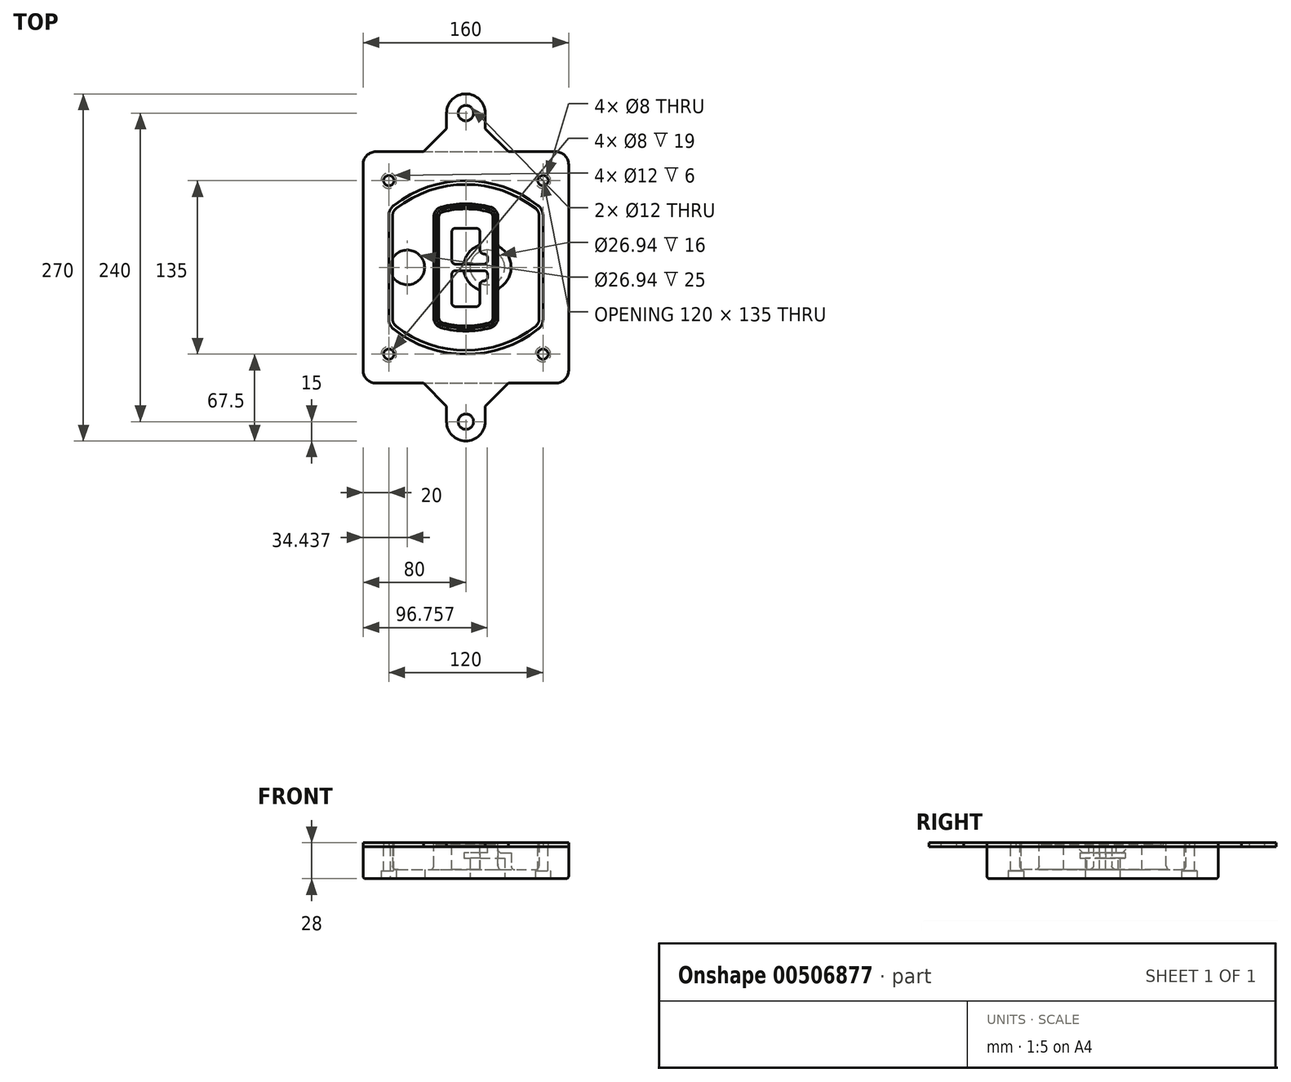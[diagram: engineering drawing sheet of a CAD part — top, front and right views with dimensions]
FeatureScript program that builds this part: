
annotation { "Feature Type Name" : "Feature", "Feature Type Description" : "" }
export const myFeature = defineFeature(function(context is Context, id is Id, definition is map)
    precondition{}
    {
        {
            var Q0;
            Q0=qCreatedBy(makeId("Top.planeOp"),FACE);
            var sketch = newSketch(context, id + "F0", { "sketchPlane" : qUnion([Q0])});
            skPoint(sketch, "E0.rect.middle", {"position": v(0, 0) * mm});
            skLineSegment(sketch, "E1.bottom", {"start": v(-70, -90) * mm, "end": v(70, -90) * mm});
            skLineSegment(sketch, "E1.top", {"start": v(-70, 90) * mm, "end": v(70, 90) * mm});
            skLineSegment(sketch, "E1.left", {"start": v(-80, -80) * mm, "end": v(-80, 80) * mm});
            skLineSegment(sketch, "E1.right", {"start": v(80, -80) * mm, "end": v(80, 80) * mm});
            skLineSegment(sketch, "E2", {"start": v(-80, 90) * mm, "end": v(80, -90) * mm, "construction": true});
            skLineSegment(sketch, "E3", {"start": v(80, 90) * mm, "end": v(-80, -90) * mm, "construction": true});
            skCircle(sketch, "E4", {"center": v(-60, 67.5) * mm, "radius": 4 * mm});
            skCircle(sketch, "E5", {"center": v(60, 67.5) * mm, "radius": 4 * mm});
            skCircle(sketch, "E6", {"center": v(60, -67.5) * mm, "radius": 4 * mm});
            skCircle(sketch, "E7", {"center": v(-60, -67.5) * mm, "radius": 4 * mm});
            skLineSegment(sketch, "E8", {"start": v(-60, 67.5) * mm, "end": v(60, 67.5) * mm, "construction": true});
            skLineSegment(sketch, "E9", {"start": v(60, 67.5) * mm, "end": v(60, -67.5) * mm, "construction": true});
            skLineSegment(sketch, "E10", {"start": v(60, -67.5) * mm, "end": v(-60, -67.5) * mm, "construction": true});
            skLineSegment(sketch, "E11", {"start": v(-60, -67.5) * mm, "end": v(-60, 67.5) * mm, "construction": true});
            skLineSegment(sketch, "E12", {"start": v(-60, 40.3) * mm, "end": v(-60, -40.3) * mm});
            skLineSegment(sketch, "E13", {"start": v(60, 40.3) * mm, "end": v(60, -40.3) * mm});
            skArc(sketch, "E14", {"start": v(56.15, 48.18) * mm, "mid": v(0, 67.5) * mm, "end": v(-56.15, 48.18) * mm});
            skArc(sketch, "E15", {"start": v(-56.15, -48.18) * mm, "mid": v(0, -67.5) * mm, "end": v(56.15, -48.18) * mm});
            skLineSegment(sketch, "E16", {"start": v(-60, 0) * mm, "end": v(60, 0) * mm, "construction": true});
            skPoint(sketch, "E17.visualSharp", {"position": v(-60, -45) * mm});
            skArc(sketch, "E17.filletArc", {"start": v(-60, -40.3) * mm, "mid": v(-58.99, -44.68) * mm, "end": v(-56.15, -48.18) * mm});
            skPoint(sketch, "E18.visualSharp", {"position": v(-60, 45) * mm});
            skArc(sketch, "E18.filletArc", {"start": v(-56.15, 48.18) * mm, "mid": v(-58.99, 44.68) * mm, "end": v(-60, 40.3) * mm});
            skPoint(sketch, "E19.visualSharp", {"position": v(60, 45) * mm});
            skArc(sketch, "E19.filletArc", {"start": v(60, 40.3) * mm, "mid": v(58.99, 44.68) * mm, "end": v(56.15, 48.18) * mm});
            skPoint(sketch, "E20.visualSharp", {"position": v(60, -45) * mm});
            skArc(sketch, "E20.filletArc", {"start": v(56.15, -48.18) * mm, "mid": v(58.99, -44.68) * mm, "end": v(60, -40.3) * mm});
            skPoint(sketch, "E21.visualSharp", {"position": v(-80, 90) * mm});
            skArc(sketch, "E21.filletArc", {"start": v(-70, 90) * mm, "mid": v(-77.07, 87.07) * mm, "end": v(-80, 80) * mm});
            skPoint(sketch, "E22.visualSharp", {"position": v(80, 90) * mm});
            skArc(sketch, "E22.filletArc", {"start": v(80, 80) * mm, "mid": v(77.07, 87.07) * mm, "end": v(70, 90) * mm});
            skPoint(sketch, "E23.visualSharp", {"position": v(80, -90) * mm});
            skArc(sketch, "E23.filletArc", {"start": v(70, -90) * mm, "mid": v(77.07, -87.07) * mm, "end": v(80, -80) * mm});
            skPoint(sketch, "E24.visualSharp", {"position": v(-80, -90) * mm});
            skArc(sketch, "E24.filletArc", {"start": v(-80, -80) * mm, "mid": v(-77.07, -87.07) * mm, "end": v(-70, -90) * mm});
            skArc(sketch, "E25.0", {"start": v(57, 40.3) * mm, "mid": v(56.3, 43.36) * mm, "end": v(54.3, 45.81) * mm});
            skLineSegment(sketch, "E25.1", {"start": v(57, 40.3) * mm, "end": v(57, -40.3) * mm});
            skArc(sketch, "E25.2", {"start": v(54.3, -45.81) * mm, "mid": v(56.3, -43.36) * mm, "end": v(57, -40.3) * mm});
            skArc(sketch, "E25.3", {"start": v(-54.3, -45.81) * mm, "mid": v(0, -64.5) * mm, "end": v(54.3, -45.81) * mm});
            skArc(sketch, "E25.4", {"start": v(-57, -40.3) * mm, "mid": v(-56.3, -43.36) * mm, "end": v(-54.3, -45.81) * mm});
            skArc(sketch, "E25.5", {"start": v(54.3, 45.81) * mm, "mid": v(0, 64.5) * mm, "end": v(-54.3, 45.81) * mm});
            skLineSegment(sketch, "E25.6", {"start": v(-57, 40.3) * mm, "end": v(-57, -40.3) * mm});
            skArc(sketch, "E25.7", {"start": v(-54.3, 45.81) * mm, "mid": v(-56.3, 43.36) * mm, "end": v(-57, 40.3) * mm});
            skArc(sketch, "E26.0", {"start": v(-58.62, 51.33) * mm, "mid": v(-62.58, 46.43) * mm, "end": v(-64, 40.3) * mm});
            skArc(sketch, "E26.1", {"start": v(58.62, 51.33) * mm, "mid": v(0, 71.5) * mm, "end": v(-58.62, 51.33) * mm});
            skArc(sketch, "E26.2", {"start": v(64, 40.3) * mm, "mid": v(62.58, 46.43) * mm, "end": v(58.62, 51.33) * mm});
            skLineSegment(sketch, "E26.3", {"start": v(64, 40.3) * mm, "end": v(64, -40.3) * mm});
            skArc(sketch, "E26.4", {"start": v(58.62, -51.33) * mm, "mid": v(62.58, -46.43) * mm, "end": v(64, -40.3) * mm});
            skLineSegment(sketch, "E26.5", {"start": v(-64, 40.3) * mm, "end": v(-64, -40.3) * mm});
            skArc(sketch, "E26.6", {"start": v(-58.62, -51.33) * mm, "mid": v(0, -71.5) * mm, "end": v(58.62, -51.33) * mm});
            skArc(sketch, "E26.7", {"start": v(-64, -40.3) * mm, "mid": v(-62.58, -46.43) * mm, "end": v(-58.62, -51.33) * mm});
            skSolve(sketch);
        }
        {
            var Q0;
            Q0=makeQuery(id+"F0.imprint","IMPRINT",FACE,{"disambiguationData":[TD([[makeQuery(id+"F0.imprint","IMPRINT",EDGE,{"derivedFrom":sQuery(id+"F0.wireOp",EDGE,"E1.bottom")}),1.0]])]});
            var Q1;
            Q1=makeQuery(id+"F0.imprint","IMPRINT",FACE,{"disambiguationData":[TD([[makeQuery(id+"F0.imprint","IMPRINT",EDGE,{"derivedFrom":sQuery(id+"F0.wireOp",EDGE,"E12")}),1.0]])]});
            var Q2;
            Q2=makeQuery(id+"F0.imprint","IMPRINT",FACE,{"disambiguationData":[TD([[makeQuery(id+"F0.imprint","IMPRINT",EDGE,{"derivedFrom":sQuery(id+"F0.wireOp",EDGE,"E25.0")}),1.0]])]});
            var Q3;
            Q3=makeQuery(id+"F0.imprint","IMPRINT",FACE,{"disambiguationData":[TD([[makeQuery(id+"F0.imprint","IMPRINT",EDGE,{"derivedFrom":sQuery(id+"F0.wireOp",EDGE,"E12")}),-1.0]])]});
            extrude(context, id + "F1", {"entities" : qUnion([Q0, Q1, Q2, Q3]), "oppositeDirection" : true, "depth" : 25 * mm});
        }
        {
            var Q0;
            Q0=makeQuery(id+"F0.imprint","IMPRINT",FACE,{"disambiguationData":[TD([[makeQuery(id+"F0.imprint","IMPRINT",EDGE,{"derivedFrom":sQuery(id+"F0.wireOp",EDGE,"E12")}),1.0]])]});
            extrude(context, id + "F2", {"entities" : qUnion([Q0]), "operationType" : NewBodyOperationType.ADD, "depth" : 3 * mm});
        }
        {
            var Q0;
            Q0=makeQuery(id+"F0.imprint","IMPRINT",FACE,{"disambiguationData":[TD([[makeQuery(id+"F0.imprint","IMPRINT",EDGE,{"derivedFrom":sQuery(id+"F0.wireOp",EDGE,"E25.0")}),1.0]])]});
            extrude(context, id + "F3", {"entities" : qUnion([Q0]), "operationType" : NewBodyOperationType.REMOVE, "oppositeDirection" : true, "depth" : 18 * mm});
        }
        {
            var Q0;
            Q0=makeQuery(id+"F2.opExtrude","CAP_FACE",FACE,{"disambiguationData":[OSD([sQuery(id+"F0.wireOp",EDGE,"E12"),sQuery(id+"F0.wireOp",EDGE,"E13"),sQuery(id+"F0.wireOp",EDGE,"E14"),sQuery(id+"F0.wireOp",EDGE,"E15"),sQuery(id+"F0.wireOp",EDGE,"E17.filletArc"),sQuery(id+"F0.wireOp",EDGE,"E18.filletArc"),sQuery(id+"F0.wireOp",EDGE,"E19.filletArc"),sQuery(id+"F0.wireOp",EDGE,"E20.filletArc"),sQuery(id+"F0.wireOp",EDGE,"E25.0"),sQuery(id+"F0.wireOp",EDGE,"E25.1"),sQuery(id+"F0.wireOp",EDGE,"E25.2"),sQuery(id+"F0.wireOp",EDGE,"E25.3"),sQuery(id+"F0.wireOp",EDGE,"E25.4"),sQuery(id+"F0.wireOp",EDGE,"E25.5"),sQuery(id+"F0.wireOp",EDGE,"E25.6"),sQuery(id+"F0.wireOp",EDGE,"E25.7")])],"isStart":false});
            var sketch = newSketch(context, id + "F4", { "sketchPlane" : qUnion([Q0])});
            skArc(sketch, "E27.0", {"start": v(-19.08, -46.97) * mm, "mid": v(0, -49.5) * mm, "end": v(19.08, -46.97) * mm});
            skArc(sketch, "E28.0", {"start": v(19.08, 46.97) * mm, "mid": v(0, 49.5) * mm, "end": v(-19.08, 46.97) * mm});
            skLineSegment(sketch, "E29", {"start": v(-25, 39.25) * mm, "end": v(-25, -39.25) * mm});
            skLineSegment(sketch, "E30", {"start": v(25, 39.25) * mm, "end": v(25, -39.25) * mm});
            skLineSegment(sketch, "E31", {"start": v(-25, 45.1) * mm, "end": v(25, 45.1) * mm, "construction": true});
            skLineSegment(sketch, "E32", {"start": v(-25, -45.1) * mm, "end": v(25, -45.1) * mm, "construction": true});
            skPoint(sketch, "E33.visualSharp", {"position": v(-25, 45.1) * mm});
            skArc(sketch, "E33.filletArc", {"start": v(-19.08, 46.97) * mm, "mid": v(-23.35, 44.11) * mm, "end": v(-25, 39.25) * mm});
            skPoint(sketch, "E34.visualSharp", {"position": v(25, 45.1) * mm});
            skArc(sketch, "E34.filletArc", {"start": v(25, 39.25) * mm, "mid": v(23.35, 44.11) * mm, "end": v(19.08, 46.97) * mm});
            skPoint(sketch, "E35.visualSharp", {"position": v(25, -45.1) * mm});
            skArc(sketch, "E35.filletArc", {"start": v(19.08, -46.97) * mm, "mid": v(23.35, -44.11) * mm, "end": v(25, -39.25) * mm});
            skPoint(sketch, "E36.visualSharp", {"position": v(-25, -45.1) * mm});
            skArc(sketch, "E36.filletArc", {"start": v(-25, -39.25) * mm, "mid": v(-23.35, -44.11) * mm, "end": v(-19.08, -46.97) * mm});
            skArc(sketch, "E37.0", {"start": v(54.3, 45.81) * mm, "mid": v(0, 64.5) * mm, "end": v(-54.3, 45.81) * mm});
            skArc(sketch, "E37.1", {"start": v(-54.3, 45.81) * mm, "mid": v(-56.3, 43.36) * mm, "end": v(-57, 40.3) * mm});
            skLineSegment(sketch, "E37.2", {"start": v(-57, 40.3) * mm, "end": v(-57, -40.3) * mm});
            skArc(sketch, "E37.3", {"start": v(-57, -40.3) * mm, "mid": v(-56.3, -43.36) * mm, "end": v(-54.3, -45.81) * mm});
            skArc(sketch, "E37.4", {"start": v(-54.3, -45.81) * mm, "mid": v(0, -64.5) * mm, "end": v(54.3, -45.81) * mm});
            skArc(sketch, "E37.5", {"start": v(54.3, -45.81) * mm, "mid": v(56.3, -43.36) * mm, "end": v(57, -40.3) * mm});
            skLineSegment(sketch, "E37.6", {"start": v(57, 40.3) * mm, "end": v(57, -40.3) * mm});
            skArc(sketch, "E37.7", {"start": v(57, 40.3) * mm, "mid": v(56.3, 43.36) * mm, "end": v(54.3, 45.81) * mm});
            skLineSegment(sketch, "E38.0", {"start": v(23, 39.25) * mm, "end": v(23, -39.25) * mm});
            skArc(sketch, "E38.1", {"start": v(18.56, -45.04) * mm, "mid": v(21.76, -42.9) * mm, "end": v(23, -39.25) * mm});
            skArc(sketch, "E38.2", {"start": v(-18.56, -45.04) * mm, "mid": v(0, -47.5) * mm, "end": v(18.56, -45.04) * mm});
            skArc(sketch, "E38.3", {"start": v(-23, -39.25) * mm, "mid": v(-21.76, -42.9) * mm, "end": v(-18.56, -45.04) * mm});
            skLineSegment(sketch, "E38.4", {"start": v(-23, 39.25) * mm, "end": v(-23, -39.25) * mm});
            skArc(sketch, "E38.5", {"start": v(23, 39.25) * mm, "mid": v(21.76, 42.9) * mm, "end": v(18.56, 45.04) * mm});
            skArc(sketch, "E38.6", {"start": v(-18.56, 45.04) * mm, "mid": v(-21.76, 42.9) * mm, "end": v(-23, 39.25) * mm});
            skArc(sketch, "E38.7", {"start": v(18.56, 45.04) * mm, "mid": v(0, 47.5) * mm, "end": v(-18.56, 45.04) * mm});
            skArc(sketch, "E39.0", {"start": v(21, 39.25) * mm, "mid": v(20.18, 41.68) * mm, "end": v(18.04, 43.1) * mm});
            skLineSegment(sketch, "E39.1", {"start": v(21, 39.25) * mm, "end": v(21, -39.25) * mm});
            skArc(sketch, "E39.2", {"start": v(18.04, -43.1) * mm, "mid": v(20.18, -41.68) * mm, "end": v(21, -39.25) * mm});
            skArc(sketch, "E39.3", {"start": v(-18.04, -43.1) * mm, "mid": v(0, -45.5) * mm, "end": v(18.04, -43.1) * mm});
            skArc(sketch, "E39.4", {"start": v(-21, -39.25) * mm, "mid": v(-20.18, -41.68) * mm, "end": v(-18.04, -43.1) * mm});
            skArc(sketch, "E39.5", {"start": v(18.04, 43.1) * mm, "mid": v(0, 45.5) * mm, "end": v(-18.04, 43.1) * mm});
            skLineSegment(sketch, "E39.6", {"start": v(-21, 39.25) * mm, "end": v(-21, -39.25) * mm});
            skArc(sketch, "E39.7", {"start": v(-18.04, 43.1) * mm, "mid": v(-20.18, 41.68) * mm, "end": v(-21, 39.25) * mm});
            skLineSegment(sketch, "E40", {"start": v(-25, 0) * mm, "end": v(25, 0) * mm, "construction": true});
            skLineSegment(sketch, "E41", {"start": v(-11, 5.5) * mm, "end": v(-11, 27.5) * mm});
            skLineSegment(sketch, "E42", {"start": v(-8, 30.5) * mm, "end": v(8, 30.5) * mm});
            skLineSegment(sketch, "E43", {"start": v(11, 27.5) * mm, "end": v(11, 13.5) * mm});
            skLineSegment(sketch, "E44", {"start": v(14, 10.5) * mm, "end": v(14, 10.5) * mm});
            skLineSegment(sketch, "E45", {"start": v(17, 7.5) * mm, "end": v(17, 5.5) * mm});
            skLineSegment(sketch, "E46", {"start": v(14, 2.5) * mm, "end": v(-8, 2.5) * mm});
            skPoint(sketch, "E47.visualSharp", {"position": v(-11, 30.5) * mm});
            skArc(sketch, "E47.filletArc", {"start": v(-8, 30.5) * mm, "mid": v(-10.12, 29.62) * mm, "end": v(-11, 27.5) * mm});
            skPoint(sketch, "E48.visualSharp", {"position": v(11, 30.5) * mm});
            skArc(sketch, "E48.filletArc", {"start": v(11, 27.5) * mm, "mid": v(10.12, 29.62) * mm, "end": v(8, 30.5) * mm});
            skPoint(sketch, "E49.visualSharp", {"position": v(11, 10.5) * mm});
            skArc(sketch, "E49.filletArc", {"start": v(11, 13.5) * mm, "mid": v(11.88, 11.38) * mm, "end": v(14, 10.5) * mm});
            skPoint(sketch, "E50.visualSharp", {"position": v(17, 10.5) * mm});
            skArc(sketch, "E50.filletArc", {"start": v(17, 7.5) * mm, "mid": v(16.12, 9.62) * mm, "end": v(14, 10.5) * mm});
            skPoint(sketch, "E51.visualSharp", {"position": v(17, 2.5) * mm});
            skArc(sketch, "E51.filletArc", {"start": v(14, 2.5) * mm, "mid": v(16.12, 3.38) * mm, "end": v(17, 5.5) * mm});
            skPoint(sketch, "E52.visualSharp", {"position": v(-11, 2.5) * mm});
            skArc(sketch, "E52.filletArc", {"start": v(-11, 5.5) * mm, "mid": v(-10.12, 3.38) * mm, "end": v(-8, 2.5) * mm});
            skLineSegment(sketch, "E53.0.MirrorCS", {"start": v(14, -2.5) * mm, "end": v(-8, -2.5) * mm});
            skArc(sketch, "E54.0.MirrorCS", {"start": v(-11, -5.5) * mm, "mid": v(-10.12, -3.38) * mm, "end": v(-8, -2.5) * mm});
            skLineSegment(sketch, "E55.0.MirrorCS", {"start": v(-11, -5.5) * mm, "end": v(-11, -27.5) * mm});
            skArc(sketch, "E56.0.MirrorCS", {"start": v(-8, -30.5) * mm, "mid": v(-10.12, -29.62) * mm, "end": v(-11, -27.5) * mm});
            skLineSegment(sketch, "E57.0.MirrorCS", {"start": v(-8, -30.5) * mm, "end": v(8, -30.5) * mm});
            skArc(sketch, "E58.0.MirrorCS", {"start": v(11, -27.5) * mm, "mid": v(10.12, -29.62) * mm, "end": v(8, -30.5) * mm});
            skLineSegment(sketch, "E59.0.MirrorCS", {"start": v(11, -27.5) * mm, "end": v(11, -13.5) * mm});
            skArc(sketch, "E60.0.MirrorCS", {"start": v(11, -13.5) * mm, "mid": v(11.88, -11.38) * mm, "end": v(14, -10.5) * mm});
            skArc(sketch, "E61.0.MirrorCS", {"start": v(17, -7.5) * mm, "mid": v(16.12, -9.62) * mm, "end": v(14, -10.5) * mm});
            skLineSegment(sketch, "E62.0.MirrorCS", {"start": v(17, -7.5) * mm, "end": v(17, -5.5) * mm});
            skArc(sketch, "E63.0.MirrorCS", {"start": v(14, -2.5) * mm, "mid": v(16.12, -3.38) * mm, "end": v(17, -5.5) * mm});
            skSolve(sketch);
        }
        {
            var Q0;
            Q0=makeQuery(id+"F4.imprint","IMPRINT",FACE,{"disambiguationData":[TD([[makeQuery(id+"F4.imprint","IMPRINT",EDGE,{"derivedFrom":sQuery(id+"F4.wireOp",EDGE,"E27.0")}),1.0]])]});
            var Q1;
            Q1=makeQuery(id+"F4.imprint","IMPRINT",FACE,{"disambiguationData":[TD([[makeQuery(id+"F4.imprint","IMPRINT",EDGE,{"derivedFrom":sQuery(id+"F4.wireOp",EDGE,"E38.0")}),-1.0]])]});
            var Q2;
            Q2=makeQuery(id+"F4.imprint","IMPRINT",FACE,{"disambiguationData":[TD([[makeQuery(id+"F4.imprint","IMPRINT",EDGE,{"derivedFrom":sQuery(id+"F4.wireOp",EDGE,"E39.0")}),1.0]])]});
            extrude(context, id + "F5", {"entities" : qUnion([Q0, Q1, Q2]), "operationType" : NewBodyOperationType.ADD, "endBound" : BoundingType.UP_TO_NEXT, "oppositeDirection" : true, "depth" : 25 * mm});
        }
        {
            var Q0;
            Q0=makeQuery(id+"F4.imprint","IMPRINT",FACE,{"disambiguationData":[TD([[makeQuery(id+"F4.imprint","IMPRINT",EDGE,{"derivedFrom":sQuery(id+"F4.wireOp",EDGE,"E38.0")}),-1.0]])]});
            extrude(context, id + "F6", {"entities" : qUnion([Q0]), "operationType" : NewBodyOperationType.REMOVE, "oppositeDirection" : true, "depth" : 2 * mm});
        }
        {
            var Q0;
            Q0=makeQuery(id+"F1.opExtrude","CAP_FACE",FACE,{"disambiguationData":[OSD([sQuery(id+"F0.wireOp",EDGE,"E1.bottom"),sQuery(id+"F0.wireOp",EDGE,"E1.top"),sQuery(id+"F0.wireOp",EDGE,"E1.left"),sQuery(id+"F0.wireOp",EDGE,"E1.right"),sQuery(id+"F0.wireOp",EDGE,"E4"),sQuery(id+"F0.wireOp",EDGE,"E5"),sQuery(id+"F0.wireOp",EDGE,"E6"),sQuery(id+"F0.wireOp",EDGE,"E7"),sQuery(id+"F0.wireOp",EDGE,"E21.filletArc"),sQuery(id+"F0.wireOp",EDGE,"E22.filletArc"),sQuery(id+"F0.wireOp",EDGE,"E23.filletArc"),sQuery(id+"F0.wireOp",EDGE,"E24.filletArc")])],"isStart":false});
            var sketch = newSketch(context, id + "F7", { "sketchPlane" : qUnion([Q0])});
            skCircle(sketch, "E64", {"center": v(16.76, 0) * mm, "radius": 13.47 * mm});
            skCircle(sketch, "E65", {"center": v(-45.56, 0) * mm, "radius": 13.47 * mm});
            skLineSegment(sketch, "E66", {"start": v(80, 0) * mm, "end": v(-80, 0) * mm});
            skCircle(sketch, "E67", {"center": v(16.76, 0) * mm, "radius": 18.47 * mm});
            skCircle(sketch, "E68", {"center": v(60, -67.5) * mm, "radius": 6 * mm});
            skCircle(sketch, "E69", {"center": v(-60, -67.5) * mm, "radius": 6 * mm});
            skCircle(sketch, "E70", {"center": v(-60, 67.5) * mm, "radius": 6 * mm});
            skCircle(sketch, "E71", {"center": v(60, 67.5) * mm, "radius": 6 * mm});
            skSolve(sketch);
        }
        {
            var Q0;
            {var subQ1=sQuery(id+"F7.wireOp",EDGE,"E66");var subQ4=sQuery(id+"F7.wireOp",EDGE,"E64");var subQ6=makeQuery(id+"F7.imprint","INTERSECT",VERTEX,{"disambiguationData":[OD(0.0)],"derivedFrom":[subQ4,subQ1]});Q0=makeQuery(id+"F7.imprint","IMPRINT",FACE,{"disambiguationData":[TD([[makeQuery(id+"F7.imprint","IMPRINT",EDGE,{"disambiguationData":[TD([[subQ6,-1.0]])],"derivedFrom":subQ4}),-1.0]])]});}
            var Q1;
            {var subQ0=sQuery(id+"F7.wireOp",EDGE,"E66");var subQ1=sQuery(id+"F7.wireOp",EDGE,"E64");var subQ3=makeQuery(id+"F7.imprint","INTERSECT",VERTEX,{"disambiguationData":[OD(0.0)],"derivedFrom":[subQ1,subQ0]});Q1=makeQuery(id+"F7.imprint","IMPRINT",FACE,{"disambiguationData":[TD([[makeQuery(id+"F7.imprint","IMPRINT",EDGE,{"disambiguationData":[TD([[subQ3,-1.0]])],"derivedFrom":subQ1}),1.0]])]});}
            var Q2;
            {var subQ0=sQuery(id+"F7.wireOp",EDGE,"E66");var subQ1=sQuery(id+"F7.wireOp",EDGE,"E64");var subQ3=makeQuery(id+"F7.imprint","INTERSECT",VERTEX,{"disambiguationData":[OD(0.0)],"derivedFrom":[subQ1,subQ0]});Q2=makeQuery(id+"F7.imprint","IMPRINT",FACE,{"disambiguationData":[TD([[makeQuery(id+"F7.imprint","IMPRINT",EDGE,{"disambiguationData":[TD([[subQ3,1.0]])],"derivedFrom":subQ1}),1.0]])]});}
            var Q3;
            {var subQ1=sQuery(id+"F7.wireOp",EDGE,"E66");var subQ4=sQuery(id+"F7.wireOp",EDGE,"E64");var subQ6=makeQuery(id+"F7.imprint","INTERSECT",VERTEX,{"disambiguationData":[OD(0.0)],"derivedFrom":[subQ4,subQ1]});Q3=makeQuery(id+"F7.imprint","IMPRINT",FACE,{"disambiguationData":[TD([[makeQuery(id+"F7.imprint","IMPRINT",EDGE,{"disambiguationData":[TD([[subQ6,1.0]])],"derivedFrom":subQ4}),-1.0]])]});}
            extrude(context, id + "F8", {"entities" : qUnion([Q0, Q1, Q2, Q3]), "operationType" : NewBodyOperationType.ADD, "oppositeDirection" : true, "depth" : 20 * mm});
        }
        {
            var Q0;
            {var subQ0=sQuery(id+"F7.wireOp",EDGE,"E66");var subQ1=sQuery(id+"F7.wireOp",EDGE,"E64");var subQ3=makeQuery(id+"F7.imprint","INTERSECT",VERTEX,{"disambiguationData":[OD(0.0)],"derivedFrom":[subQ1,subQ0]});Q0=makeQuery(id+"F7.imprint","IMPRINT",FACE,{"disambiguationData":[TD([[makeQuery(id+"F7.imprint","IMPRINT",EDGE,{"disambiguationData":[TD([[subQ3,-1.0]])],"derivedFrom":subQ1}),1.0]])]});}
            var Q1;
            {var subQ0=sQuery(id+"F7.wireOp",EDGE,"E66");var subQ1=sQuery(id+"F7.wireOp",EDGE,"E64");var subQ3=makeQuery(id+"F7.imprint","INTERSECT",VERTEX,{"disambiguationData":[OD(0.0)],"derivedFrom":[subQ1,subQ0]});Q1=makeQuery(id+"F7.imprint","IMPRINT",FACE,{"disambiguationData":[TD([[makeQuery(id+"F7.imprint","IMPRINT",EDGE,{"disambiguationData":[TD([[subQ3,1.0]])],"derivedFrom":subQ1}),1.0]])]});}
            extrude(context, id + "F9", {"entities" : qUnion([Q0, Q1]), "operationType" : NewBodyOperationType.REMOVE, "oppositeDirection" : true, "depth" : 16 * mm});
        }
        {
            var Q0;
            {var subQ0=sQuery(id+"F7.wireOp",EDGE,"E66");var subQ1=sQuery(id+"F7.wireOp",EDGE,"E65");var subQ3=makeQuery(id+"F7.imprint","INTERSECT",VERTEX,{"disambiguationData":[OD(0.0)],"derivedFrom":[subQ1,subQ0]});Q0=makeQuery(id+"F7.imprint","IMPRINT",FACE,{"disambiguationData":[TD([[makeQuery(id+"F7.imprint","IMPRINT",EDGE,{"disambiguationData":[TD([[subQ3,-1.0]])],"derivedFrom":subQ1}),1.0]])]});}
            var Q1;
            {var subQ0=sQuery(id+"F7.wireOp",EDGE,"E66");var subQ1=sQuery(id+"F7.wireOp",EDGE,"E65");var subQ3=makeQuery(id+"F7.imprint","INTERSECT",VERTEX,{"disambiguationData":[OD(0.0)],"derivedFrom":[subQ1,subQ0]});Q1=makeQuery(id+"F7.imprint","IMPRINT",FACE,{"disambiguationData":[TD([[makeQuery(id+"F7.imprint","IMPRINT",EDGE,{"disambiguationData":[TD([[subQ3,1.0]])],"derivedFrom":subQ1}),1.0]])]});}
            extrude(context, id + "F10", {"entities" : qUnion([Q0, Q1]), "operationType" : NewBodyOperationType.REMOVE, "oppositeDirection" : true, "depth" : 25 * mm});
        }
        {
            var Q0;
            Q0=makeQuery(id+"F7.imprint","IMPRINT",FACE,{"disambiguationData":[TD([[makeQuery(id+"F7.imprint","IMPRINT",EDGE,{"derivedFrom":sQuery(id+"F7.wireOp",EDGE,"E68")}),1.0]])]});
            var Q1;
            Q1=makeQuery(id+"F7.imprint","IMPRINT",FACE,{"disambiguationData":[TD([[makeQuery(id+"F7.imprint","IMPRINT",EDGE,{"derivedFrom":makeQuery(id+"F1.opExtrude","CAP_EDGE",EDGE,{"disambiguationData":[OSD([sQuery(id+"F0.wireOp",EDGE,"E5")])],"isStart":false})}),-1.0]])]});
            var Q2;
            Q2=makeQuery(id+"F7.imprint","IMPRINT",FACE,{"disambiguationData":[TD([[makeQuery(id+"F7.imprint","IMPRINT",EDGE,{"derivedFrom":sQuery(id+"F7.wireOp",EDGE,"E69")}),1.0]])]});
            var Q3;
            Q3=makeQuery(id+"F7.imprint","IMPRINT",FACE,{"disambiguationData":[TD([[makeQuery(id+"F7.imprint","IMPRINT",EDGE,{"derivedFrom":makeQuery(id+"F1.opExtrude","CAP_EDGE",EDGE,{"disambiguationData":[OSD([sQuery(id+"F0.wireOp",EDGE,"E4")])],"isStart":false})}),-1.0]])]});
            var Q4;
            Q4=makeQuery(id+"F7.imprint","IMPRINT",FACE,{"disambiguationData":[TD([[makeQuery(id+"F7.imprint","IMPRINT",EDGE,{"derivedFrom":sQuery(id+"F7.wireOp",EDGE,"E70")}),1.0]])]});
            var Q5;
            Q5=makeQuery(id+"F7.imprint","IMPRINT",FACE,{"disambiguationData":[TD([[makeQuery(id+"F7.imprint","IMPRINT",EDGE,{"derivedFrom":makeQuery(id+"F1.opExtrude","CAP_EDGE",EDGE,{"disambiguationData":[OSD([sQuery(id+"F0.wireOp",EDGE,"E7")])],"isStart":false})}),-1.0]])]});
            var Q6;
            Q6=makeQuery(id+"F7.imprint","IMPRINT",FACE,{"disambiguationData":[TD([[makeQuery(id+"F7.imprint","IMPRINT",EDGE,{"derivedFrom":sQuery(id+"F7.wireOp",EDGE,"E71")}),1.0]])]});
            var Q7;
            Q7=makeQuery(id+"F7.imprint","IMPRINT",FACE,{"disambiguationData":[TD([[makeQuery(id+"F7.imprint","IMPRINT",EDGE,{"derivedFrom":makeQuery(id+"F1.opExtrude","CAP_EDGE",EDGE,{"disambiguationData":[OSD([sQuery(id+"F0.wireOp",EDGE,"E6")])],"isStart":false})}),-1.0]])]});
            extrude(context, id + "F11", {"entities" : qUnion([Q0, Q1, Q2, Q3, Q4, Q5, Q6, Q7]), "operationType" : NewBodyOperationType.REMOVE, "oppositeDirection" : true, "depth" : 6 * mm});
        }
        {
            var Q0;
            Q0=makeQuery(id+"F9.boolean.opBoolean","COPY",FACE,{"derivedFrom":makeQuery(id+"F9.opExtrude","CAP_FACE",FACE,{"disambiguationData":[OSD([sQuery(id+"F7.wireOp",EDGE,"E64")])],"isStart":false})});
            var sketch = newSketch(context, id + "F12", { "sketchPlane" : qUnion([Q0])});
            skArc(sketch, "E72.0", {"start": v(11, 17.55) * mm, "mid": v(2.57, 11.82) * mm, "end": v(-1.54, 2.5) * mm});
            skArc(sketch, "E72.1", {"start": v(-1.54, -2.5) * mm, "mid": v(2.57, -11.82) * mm, "end": v(11, -17.55) * mm});
            skLineSegment(sketch, "E73", {"start": v(-1.54, -2.5) * mm, "end": v(14, -2.5) * mm});
            skLineSegment(sketch, "E74.0", {"start": v(14, 2.5) * mm, "end": v(-1.54, 2.5) * mm});
            skArc(sketch, "E74.1", {"start": v(14, 2.5) * mm, "mid": v(16.12, 3.38) * mm, "end": v(17, 5.5) * mm});
            skLineSegment(sketch, "E74.2", {"start": v(17, 7.5) * mm, "end": v(17, 5.5) * mm});
            skArc(sketch, "E74.3", {"start": v(17, 7.5) * mm, "mid": v(16.12, 9.62) * mm, "end": v(14, 10.5) * mm});
            skArc(sketch, "E74.4", {"start": v(11, 13.5) * mm, "mid": v(11.88, 11.38) * mm, "end": v(14, 10.5) * mm});
            skLineSegment(sketch, "E74.5", {"start": v(11, 17.55) * mm, "end": v(11, 13.5) * mm});
            skLineSegment(sketch, "E74.7", {"start": v(14, -2.5) * mm, "end": v(-1.54, -2.5) * mm});
            skArc(sketch, "E74.8", {"start": v(14, -2.5) * mm, "mid": v(16.12, -3.38) * mm, "end": v(17, -5.5) * mm});
            skLineSegment(sketch, "E74.9", {"start": v(17, -7.5) * mm, "end": v(17, -5.5) * mm});
            skArc(sketch, "E74.10", {"start": v(17, -7.5) * mm, "mid": v(16.12, -9.62) * mm, "end": v(14, -10.5) * mm});
            skArc(sketch, "E74.11", {"start": v(11, -13.5) * mm, "mid": v(11.88, -11.38) * mm, "end": v(14, -10.5) * mm});
            skLineSegment(sketch, "E74.12", {"start": v(11, -17.55) * mm, "end": v(11, -13.5) * mm});
            skPoint(sketch, "E75.orphan", {"position": v(11, -27.5) * mm});
            skPoint(sketch, "E76.orphan", {"position": v(-8, -2.5) * mm});
            skPoint(sketch, "E77.orphan", {"position": v(-8, 2.5) * mm});
            skPoint(sketch, "E78.orphan", {"position": v(11, 27.5) * mm});
            skSolve(sketch);
        }
        {
            var Q0;
            {var subQ7=sQuery(id+"F12.wireOp",EDGE,"E72.0");var subQ14=sQuery(id+"F12.wireOp",EDGE,"E72.1");var subQ16=sQuery(id+"F12.wireOp",EDGE,"E74.1");var subQ18=sQuery(id+"F12.wireOp",EDGE,"E74.8");Q0=qUnion([makeQuery(id+"F12.imprint","IMPRINT",FACE,{"disambiguationData":[TD([[makeQuery(id+"F12.imprint","IMPRINT",EDGE,{"derivedFrom":subQ7}),1.0]])]}),makeQuery(id+"F12.imprint","IMPRINT",FACE,{"disambiguationData":[TD([[makeQuery(id+"F12.imprint","IMPRINT",EDGE,{"derivedFrom":subQ14}),1.0]])]}),makeQuery(id+"F12.imprint","IMPRINT",FACE,{"disambiguationData":[TD([[makeQuery(id+"F12.imprint","IMPRINT",EDGE,{"derivedFrom":subQ16}),1.0]])]}),makeQuery(id+"F12.imprint","IMPRINT",FACE,{"disambiguationData":[TD([[makeQuery(id+"F12.imprint","IMPRINT",EDGE,{"derivedFrom":subQ18}),-1.0]])]})]);}
            var Q1;
            Q1=makeQuery(id+"F5.boolean.opBoolean","SPLIT",FACE,{"disambiguationData":[TD([makeQuery(id+"F5.opExtrude","SWEPT_FACE",FACE,{"disambiguationData":[OSD([sQuery(id+"F4.wireOp",EDGE,"E41")])]})])],"derivedFrom":makeQuery(id+"F3.boolean.opBoolean","COPY",FACE,{"derivedFrom":makeQuery(id+"F3.opExtrude","CAP_FACE",FACE,{"disambiguationData":[OSD([sQuery(id+"F0.wireOp",EDGE,"E25.0"),sQuery(id+"F0.wireOp",EDGE,"E25.1"),sQuery(id+"F0.wireOp",EDGE,"E25.2"),sQuery(id+"F0.wireOp",EDGE,"E25.3"),sQuery(id+"F0.wireOp",EDGE,"E25.4"),sQuery(id+"F0.wireOp",EDGE,"E25.5"),sQuery(id+"F0.wireOp",EDGE,"E25.6"),sQuery(id+"F0.wireOp",EDGE,"E25.7")])],"isStart":false})})});
            extrude(context, id + "F13", {"entities" : qUnion([Q0]), "operationType" : NewBodyOperationType.REMOVE, "endBound" : BoundingType.UP_TO_SURFACE, "endBoundEntityFace" : qUnion([Q1]), "depth" : 25 * mm});
        }
        {
            var Q0;
            Q0=makeQuery(id+"F3.boolean.opBoolean","COPY",EDGE,{"derivedFrom":makeQuery(id+"F3.opExtrude","CAP_EDGE",EDGE,{"disambiguationData":[OSD([sQuery(id+"F0.wireOp",EDGE,"E25.6")])],"isStart":false})});
            var Q1;
            Q1=makeQuery(id+"F8.boolean.opBoolean","INTERSECT",EDGE,{"derivedFrom":[makeQuery(id+"F5.opExtrude","SWEPT_FACE",FACE,{"disambiguationData":[OSD([sQuery(id+"F4.wireOp",EDGE,"E30")])]}),makeQuery(id+"F8.opExtrude","CAP_FACE",FACE,{"disambiguationData":[OSD([sQuery(id+"F7.wireOp",EDGE,"E67")])],"isStart":false})]});
            var Q2;
            Q2=makeQuery(id+"F8.boolean.opBoolean","INTERSECT",EDGE,{"disambiguationData":[OD(1.0)],"derivedFrom":[makeQuery(id+"F5.opExtrude","SWEPT_FACE",FACE,{"disambiguationData":[OSD([sQuery(id+"F4.wireOp",EDGE,"E30")])]}),makeQuery(id+"F8.opExtrude","SWEPT_FACE",FACE,{"disambiguationData":[OSD([sQuery(id+"F7.wireOp",EDGE,"E67")])]})]});
            var Q3;
            {var subQ0=sQuery(id+"F4.wireOp",EDGE,"E30");Q3=makeQuery(id+"F8.boolean.opBoolean","SPLIT",EDGE,{"disambiguationData":[TD([makeQuery(id+"F5.opExtrude","SWEPT_FACE",FACE,{"disambiguationData":[OSD([sQuery(id+"F4.wireOp",EDGE,"E35.filletArc")])]})])],"derivedFrom":makeQuery(id+"F5.opExtrude","CAP_EDGE",EDGE,{"disambiguationData":[OSD([subQ0])],"isStart":false})});}
            var Q4;
            {var subQ0=sQuery(id+"F0.wireOp",EDGE,"E25.7");var subQ1=sQuery(id+"F0.wireOp",EDGE,"E25.1");var subQ2=sQuery(id+"F0.wireOp",EDGE,"E25.6");var subQ3=sQuery(id+"F0.wireOp",EDGE,"E25.5");var subQ4=sQuery(id+"F0.wireOp",EDGE,"E25.4");var subQ5=sQuery(id+"F0.wireOp",EDGE,"E25.0");var subQ6=sQuery(id+"F0.wireOp",EDGE,"E25.2");var subQ7=sQuery(id+"F0.wireOp",EDGE,"E25.3");Q4=makeQuery(id+"F8.boolean.opBoolean","INTERSECT",EDGE,{"derivedFrom":[makeQuery(id+"F5.boolean.opBoolean","SPLIT",FACE,{"disambiguationData":[TD([makeQuery(id+"F2.opExtrude","SWEPT_FACE",FACE,{"disambiguationData":[OSD([subQ5])]})])],"derivedFrom":makeQuery(id+"F3.boolean.opBoolean","COPY",FACE,{"derivedFrom":makeQuery(id+"F3.opExtrude","CAP_FACE",FACE,{"disambiguationData":[OSD([subQ5,subQ1,subQ6,subQ7,subQ4,subQ3,subQ2,subQ0])],"isStart":false})})}),makeQuery(id+"F8.opExtrude","SWEPT_FACE",FACE,{"disambiguationData":[OSD([sQuery(id+"F7.wireOp",EDGE,"E67")])]})]});}
            var Q5;
            Q5=makeQuery(id+"F8.boolean.opBoolean","INTERSECT",EDGE,{"disambiguationData":[OD(0.0)],"derivedFrom":[makeQuery(id+"F5.opExtrude","SWEPT_FACE",FACE,{"disambiguationData":[OSD([sQuery(id+"F4.wireOp",EDGE,"E30")])]}),makeQuery(id+"F8.opExtrude","SWEPT_FACE",FACE,{"disambiguationData":[OSD([sQuery(id+"F7.wireOp",EDGE,"E67")])]})]});
            fillet(context, id + "F14", {"entities" : qUnion([Q0, Q1, Q2, Q3, Q4, Q5]), "radius" : 3 * mm, "tangentPropagation" : true, "allowEdgeOverflow" : false});
        }
        {
            var Q0;
            Q0=makeQuery(id+"F1.opExtrude","CAP_EDGE",EDGE,{"disambiguationData":[OSD([sQuery(id+"F0.wireOp",EDGE,"E1.bottom")])],"isStart":false});
            fillet(context, id + "F15", {"entities" : qUnion([Q0]), "radius" : 2 * mm, "tangentPropagation" : true, "allowEdgeOverflow" : false});
        }
        {
            var Q0;
            {var subQ0=sQuery(id+"F0.wireOp",EDGE,"E21.filletArc");var subQ1=sQuery(id+"F0.wireOp",EDGE,"E7");var subQ2=sQuery(id+"F0.wireOp",EDGE,"E6");var subQ3=sQuery(id+"F0.wireOp",EDGE,"E5");var subQ4=sQuery(id+"F0.wireOp",EDGE,"E4");var subQ5=sQuery(id+"F0.wireOp",EDGE,"E22.filletArc");var subQ6=sQuery(id+"F0.wireOp",EDGE,"E1.bottom");var subQ7=sQuery(id+"F0.wireOp",EDGE,"E1.right");var subQ8=sQuery(id+"F0.wireOp",EDGE,"E1.top");var subQ9=sQuery(id+"F0.wireOp",EDGE,"E1.left");var subQ10=sQuery(id+"F0.wireOp",EDGE,"E23.filletArc");var subQ11=sQuery(id+"F0.wireOp",EDGE,"E24.filletArc");Q0=makeQuery(id+"F2.boolean.opBoolean","SPLIT",FACE,{"disambiguationData":[TD([makeQuery(id+"F1.opExtrude","SWEPT_FACE",FACE,{"disambiguationData":[OSD([subQ6])]})])],"derivedFrom":makeQuery(id+"F1.opExtrude","CAP_FACE",FACE,{"disambiguationData":[OSD([subQ6,subQ8,subQ9,subQ7,subQ4,subQ3,subQ2,subQ1,subQ0,subQ5,subQ10,subQ11])],"isStart":true})});}
            var sketch = newSketch(context, id + "F16", { "sketchPlane" : qUnion([Q0])});
            skCircle(sketch, "E79.0", {"center": v(-60, 67.5) * mm, "radius": 4 * mm});
            skCircle(sketch, "E79.1", {"center": v(60, 67.5) * mm, "radius": 4 * mm});
            skCircle(sketch, "E79.2", {"center": v(60, -67.5) * mm, "radius": 4 * mm});
            skCircle(sketch, "E79.3", {"center": v(-60, -67.5) * mm, "radius": 4 * mm});
            skArc(sketch, "E79.4", {"start": v(-56.15, -48.18) * mm, "mid": v(0, -67.5) * mm, "end": v(56.15, -48.18) * mm});
            skLineSegment(sketch, "E79.5", {"start": v(-60, 40.3) * mm, "end": v(-60, -40.3) * mm});
            skLineSegment(sketch, "E79.6", {"start": v(60, 40.3) * mm, "end": v(60, -40.3) * mm});
            skArc(sketch, "E79.7", {"start": v(56.15, 48.18) * mm, "mid": v(0, 67.5) * mm, "end": v(-56.15, 48.18) * mm});
            skLineSegment(sketch, "E79.8", {"start": v(80, -80) * mm, "end": v(80, 80) * mm});
            skLineSegment(sketch, "E79.9", {"start": v(-70, 90) * mm, "end": v(70, 90) * mm});
            skLineSegment(sketch, "E79.10", {"start": v(-80, -80) * mm, "end": v(-80, 80) * mm});
            skLineSegment(sketch, "E79.11", {"start": v(-70, -90) * mm, "end": v(70, -90) * mm});
            skArc(sketch, "E79.12", {"start": v(-80, -80) * mm, "mid": v(-77.07, -87.07) * mm, "end": v(-70, -90) * mm});
            skArc(sketch, "E79.13", {"start": v(70, -90) * mm, "mid": v(77.07, -87.07) * mm, "end": v(80, -80) * mm});
            skArc(sketch, "E79.14", {"start": v(80, 80) * mm, "mid": v(77.07, 87.07) * mm, "end": v(70, 90) * mm});
            skArc(sketch, "E79.15", {"start": v(-70, 90) * mm, "mid": v(-77.07, 87.07) * mm, "end": v(-80, 80) * mm});
            skArc(sketch, "E79.16", {"start": v(-56.15, 48.18) * mm, "mid": v(-58.99, 44.68) * mm, "end": v(-60, 40.3) * mm});
            skArc(sketch, "E79.17", {"start": v(60, 40.3) * mm, "mid": v(58.99, 44.68) * mm, "end": v(56.15, 48.18) * mm});
            skArc(sketch, "E79.18", {"start": v(56.15, -48.18) * mm, "mid": v(58.99, -44.68) * mm, "end": v(60, -40.3) * mm});
            skArc(sketch, "E79.19", {"start": v(-60, -40.3) * mm, "mid": v(-58.99, -44.68) * mm, "end": v(-56.15, -48.18) * mm});
            skLineSegment(sketch, "E80", {"start": v(-33, 90) * mm, "end": v(-15, 108) * mm});
            skLineSegment(sketch, "E81", {"start": v(-15, 108) * mm, "end": v(-15, 120) * mm});
            skLineSegment(sketch, "E82", {"start": v(15, 108) * mm, "end": v(33, 90) * mm});
            skLineSegment(sketch, "E83", {"start": v(15, 120) * mm, "end": v(15, 108) * mm});
            skArc(sketch, "E84", {"start": v(15, 120) * mm, "mid": v(0, 135) * mm, "end": v(-15, 120) * mm});
            skCircle(sketch, "E85", {"center": v(0, 120) * mm, "radius": 6 * mm});
            skLineSegment(sketch, "E86", {"start": v(0, 120) * mm, "end": v(0, 90) * mm, "construction": true});
            skPoint(sketch, "E87.endSnap0", {"position": v(0, -67.5) * mm});
            skLineSegment(sketch, "E88", {"start": v(80, 0) * mm, "end": v(-80, 0) * mm, "construction": true});
            skLineSegment(sketch, "E89.MirrorCS", {"start": v(-15, 108) * mm, "end": v(-33, 90) * mm});
            skLineSegment(sketch, "E90.MirrorCS", {"start": v(-15, 120) * mm, "end": v(-15, 108) * mm});
            skArc(sketch, "E91.MirrorCS", {"start": v(-15, 120) * mm, "mid": v(0, 135) * mm, "end": v(15, 120) * mm});
            skLineSegment(sketch, "E92.MirrorCS", {"start": v(-15, -108) * mm, "end": v(-33, -90) * mm});
            skLineSegment(sketch, "E93.MirrorCS", {"start": v(-15, -108) * mm, "end": v(-15, -120) * mm});
            skArc(sketch, "E94.MirrorCS", {"start": v(15, -120) * mm, "mid": v(0, -135) * mm, "end": v(-15, -120) * mm});
            skLineSegment(sketch, "E95.MirrorCS", {"start": v(15, -120) * mm, "end": v(15, -108) * mm});
            skLineSegment(sketch, "E96.MirrorCS", {"start": v(15, -108) * mm, "end": v(33, -90) * mm});
            skLineSegment(sketch, "E97.MirrorCS", {"start": v(0, -120) * mm, "end": v(0, -90) * mm, "construction": true});
            skCircle(sketch, "E98.MirrorC", {"center": v(0, -120) * mm, "radius": 6 * mm});
            skSolve(sketch);
        }
        {
            var Q0;
            Q0 = qSketchRegion(id + "F16", true);
            var Q1;
            Q1=makeQuery(id+"F2.opExtrude","CAP_FACE",FACE,{"disambiguationData":[OSD([sQuery(id+"F0.wireOp",EDGE,"E12"),sQuery(id+"F0.wireOp",EDGE,"E13"),sQuery(id+"F0.wireOp",EDGE,"E14"),sQuery(id+"F0.wireOp",EDGE,"E15"),sQuery(id+"F0.wireOp",EDGE,"E17.filletArc"),sQuery(id+"F0.wireOp",EDGE,"E18.filletArc"),sQuery(id+"F0.wireOp",EDGE,"E19.filletArc"),sQuery(id+"F0.wireOp",EDGE,"E20.filletArc"),sQuery(id+"F0.wireOp",EDGE,"E25.0"),sQuery(id+"F0.wireOp",EDGE,"E25.1"),sQuery(id+"F0.wireOp",EDGE,"E25.2"),sQuery(id+"F0.wireOp",EDGE,"E25.3"),sQuery(id+"F0.wireOp",EDGE,"E25.4"),sQuery(id+"F0.wireOp",EDGE,"E25.5"),sQuery(id+"F0.wireOp",EDGE,"E25.6"),sQuery(id+"F0.wireOp",EDGE,"E25.7")])],"isStart":false});
            extrude(context, id + "F17", {"entities" : qUnion([Q0]), "endBound" : BoundingType.UP_TO_SURFACE, "endBoundEntityFace" : qUnion([Q1]), "depth" : 25 * mm});
        }
    });
